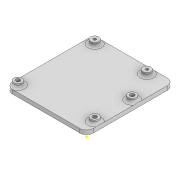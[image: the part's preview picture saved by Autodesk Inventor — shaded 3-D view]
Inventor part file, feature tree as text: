
AUTODESK INVENTOR PART (.ipt)
format: ipt  version: 2022 (Build 260153000, 153)  size: 241,664 bytes
history: native  units: mm
features: sketch x4, extrude x4, fillet x3, thicken_offset x2, chamfer x1
ambient origin geometry x8: Origin, YZ Plane, XZ Plane, XY Plane, X Axis, Y Axis, Z Axis, Center Point
bodies: Solid1 (feature_tree)
feature tree (14):
  sketch  "Sketch1"  dims[d0=60.0mm d1=65.0mm]
  extrude  "Extrusion1"  Depth=60.0mm
  extrude  "Extrusion2"  Depth=10.0mm
  fillet  "Fillet1"  Radius=10.0mm
  extrude  "Extrusion3"  Depth=4.0mm
  extrude  "Extrusion4"  Depth=15.6mm
  thicken_offset  "Thicken1"
  thicken_offset  "Thicken2"
  chamfer  "Chamfer1"  Distance=5.08mm
  fillet  "Fillet2"  Radius=27.94mm
  fillet  "Fillet3"  Radius=6.0mm
  sketch  "Sketch4"  dims[d9=3.1mm d10=52.07mm d11=5.08mm d12=27.94mm d13=6.0mm d14=6.0mm d15=6.0mm d16=6.0mm d17=0.0mm d18=2.1mm d19=60.0mm d20=54.0mm d21=6.0mm d22=2.1mm d23=6.0mm d24=38.862mm d25=2.0mm d26=3.0mm d28=18.0mm d29=18.0mm d30=3.0mm d31=3.0mm d32=8.0mm d33=0.0mm d34=3.1mm d35=3.1mm d36=4.5mm d37=4.5mm d38=4.3mm d39=4.3mm d40=10.0mm d41=0.0mm d42=0.15mm d43=0.2mm d44=0.15mm d45=0.2mm d46=8.0mm d47=2.0mm d48=45.0deg d49=5.0mm d50=1.0mm d54=15.6mm]
  sketch  "Sketch2"  dims[d2=3.0mm d3=0.0mm d4=3.1mm d5=10.0mm]
  sketch  "Sketch3"  dims[d6=3.1mm d8=4.0mm]
